# Revit family: Work_Tools-Teknion-AFWS_Focus_Wall_Sliding_Whiteboard-R2019
name_source: partatom
category: Furniture
units: mm (PartAtom-declared; Revit-internal decimal feet)

## family parameters
Always vertical = Yes
Cut with Voids When Loaded = No
OmniClass Number = 23.40.20.00
OmniClass Title = General Furniture and Specialties
Room Calculation Point = No
Shared = Yes
Work Plane-Based = No

## types (2) — shared parameters
Assembly Code = E2020200
Manufacturer = Teknion
Manufacturer Fax = 416.661.4586
Part Number = AFWS
Product Documentation Link = https://www.teknion.com
Product Line = Tables & Collaborative Spaces
Product Page URL = https://www.teknion.com
Series = Tables & Collaborative Spaces
Sustainability Data = https://www.teknion.com
URL = www.teknion.com
Unit Weight URL = http://www.teknion.com
Warranty = http://www.teknion.com

## per-type parameters (varying)
| type | Description | Height | Model |
| 42" Height | Focus Wall Sliding Whiteboard, 42" Height | 72.25 " | AFWS42__ |
| 48" Height | Focus Wall Sliding Whiteboard, 48" Height | 78.25 " | AFWS48__ |

## geometry (parser evidence)
native form markers: Sweep x3
no freeform markers — native parametric forms only
